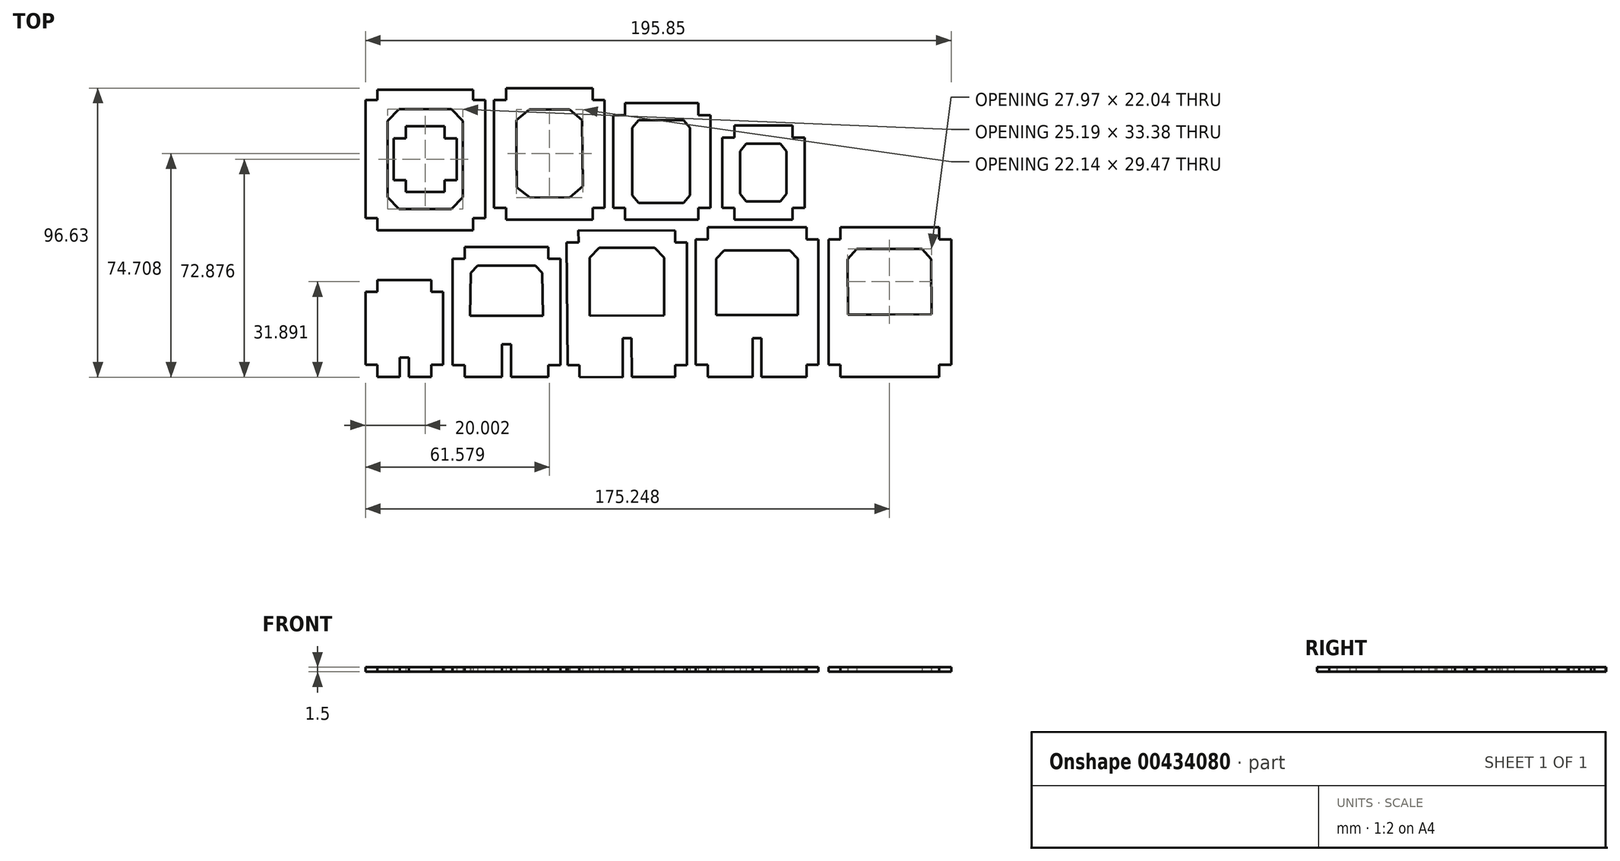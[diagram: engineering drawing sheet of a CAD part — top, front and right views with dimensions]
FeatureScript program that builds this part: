
annotation { "Feature Type Name" : "Feature", "Feature Type Description" : "" }
export const myFeature = defineFeature(function(context is Context, id is Id, definition is map)
    precondition{}
    {
        {
            var Q0;
            Q0=qCreatedBy(makeId("Top.planeOp"),FACE);
            var sketch = newSketch(context, id + "F0", { "sketchPlane" : qUnion([Q0])});
            skLineSegment(sketch, "E0", {"start": v(-112.3, 34.29) * mm, "end": v(-83.3, 34.29) * mm, "construction": true});
            skLineSegment(sketch, "E1", {"start": v(32.55, -18.26) * mm, "end": v(-0.45, -18.26) * mm, "construction": true});
            skLineSegment(sketch, "E2", {"start": v(-159.3, 74.29) * mm, "end": v(-159.3, 34.79) * mm, "construction": true});
            skLineSegment(sketch, "E3", {"start": v(-79.3, 38.29) * mm, "end": v(-79.3, 74.33) * mm, "construction": true});
            skLineSegment(sketch, "E4", {"start": v(-159.3, 74.29) * mm, "end": v(-155.3, 74.29) * mm, "construction": true});
            skLineSegment(sketch, "E5", {"start": v(-139.3, 78.29) * mm, "end": v(-139.3, 24.66) * mm, "construction": true});
            skPoint(sketch, "E5.endSnap0", {"position": v(-139.3, 74.29) * mm});
            skLineSegment(sketch, "E6", {"start": v(-155.3, 30.79) * mm, "end": v(-123.3, 30.79) * mm, "construction": true});
            skPoint(sketch, "E7.startSnap0", {"position": v(-118.3, 78.29) * mm});
            skLineSegment(sketch, "E8", {"start": v(-119.3, 74.29) * mm, "end": v(-119.3, 34.79) * mm, "construction": true});
            skPoint(sketch, "E9.0.start.orphan", {"position": v(-119.3, 78.29) * mm});
            skLineSegment(sketch, "E10.0", {"start": v(-155.3, 77.79) * mm, "end": v(-155.3, 74.29) * mm});
            skLineSegment(sketch, "E11", {"start": v(-155.3, 77.79) * mm, "end": v(-155.3, 74.29) * mm, "construction": true});
            skPoint(sketch, "E12.orphan", {"position": v(-155.3, -16.83) * mm});
            skLineSegment(sketch, "E13.trimOffspring", {"start": v(-155.3, 30.79) * mm, "end": v(-155.3, 30.48) * mm, "construction": true});
            skLineSegment(sketch, "E14.trimOffspring", {"start": v(-155.3, 30.79) * mm, "end": v(-155.3, 30.48) * mm});
            skLineSegment(sketch, "E15.MirrorCS", {"start": v(-123.3, 77.79) * mm, "end": v(-123.3, 74.29) * mm, "construction": true});
            skLineSegment(sketch, "E16.0", {"start": v(-159.3, 34.79) * mm, "end": v(-155.3, 34.79) * mm});
            skLineSegment(sketch, "E17", {"start": v(-155.3, 34.79) * mm, "end": v(-155.3, 30.48) * mm, "construction": true});
            skLineSegment(sketch, "E18", {"start": v(-123.3, 34.79) * mm, "end": v(-123.3, 30.79) * mm, "construction": true});
            skLineSegment(sketch, "E19.trimOffspring", {"start": v(-123.3, 34.79) * mm, "end": v(-119.3, 34.79) * mm});
            skLineSegment(sketch, "E20.trimOffspring", {"start": v(-123.3, 74.29) * mm, "end": v(-119.3, 74.29) * mm, "construction": true});
            skLineSegment(sketch, "E21", {"start": v(-139.3, 71.23) * mm, "end": v(-148.05, 71.23) * mm});
            skLineSegment(sketch, "E22", {"start": v(-148.05, 71.23) * mm, "end": v(-151.9, 67.31) * mm});
            skLineSegment(sketch, "E23", {"start": v(-151.9, 67.31) * mm, "end": v(-151.9, 54.54) * mm});
            skLineSegment(sketch, "E24", {"start": v(-119.3, 54.54) * mm, "end": v(-159.3, 54.54) * mm, "construction": true});
            skLineSegment(sketch, "E25.MirrorCS", {"start": v(-139.3, 71.23) * mm, "end": v(-130.55, 71.23) * mm});
            skLineSegment(sketch, "E26.MirrorCS", {"start": v(-130.55, 71.23) * mm, "end": v(-126.7, 67.31) * mm});
            skLineSegment(sketch, "E27.MirrorCS", {"start": v(-126.7, 67.31) * mm, "end": v(-126.7, 54.54) * mm});
            skLineSegment(sketch, "E28.MirrorCS", {"start": v(-139.3, 37.84) * mm, "end": v(-130.55, 37.84) * mm});
            skLineSegment(sketch, "E29.MirrorCS", {"start": v(-139.3, 37.84) * mm, "end": v(-148.05, 37.84) * mm});
            skLineSegment(sketch, "E30.MirrorCS", {"start": v(-148.05, 37.84) * mm, "end": v(-151.9, 41.76) * mm});
            skLineSegment(sketch, "E31.MirrorCS", {"start": v(-151.9, 41.76) * mm, "end": v(-151.9, 54.54) * mm});
            skLineSegment(sketch, "E32.MirrorCS", {"start": v(-126.7, 41.76) * mm, "end": v(-126.7, 54.54) * mm});
            skLineSegment(sketch, "E33.MirrorCS", {"start": v(-130.55, 37.84) * mm, "end": v(-126.7, 41.76) * mm});
            skLineSegment(sketch, "E34", {"start": v(-155.3, 77.79) * mm, "end": v(-123.3, 77.79) * mm});
            skLineSegment(sketch, "E35", {"start": v(-123.3, 74.29) * mm, "end": v(-119.3, 74.29) * mm});
            skLineSegment(sketch, "E36", {"start": v(-119.3, 34.79) * mm, "end": v(-123.3, 34.79) * mm});
            skLineSegment(sketch, "E37", {"start": v(-123.3, 30.79) * mm, "end": v(-155.3, 30.79) * mm});
            skLineSegment(sketch, "E38", {"start": v(-155.3, 34.79) * mm, "end": v(-159.3, 34.79) * mm});
            skLineSegment(sketch, "E39", {"start": v(-159.3, 74.29) * mm, "end": v(-159.3, 34.79) * mm});
            skLineSegment(sketch, "E40", {"start": v(-159.3, 74.29) * mm, "end": v(-155.3, 74.29) * mm});
            skLineSegment(sketch, "E41", {"start": v(-119.3, 74.29) * mm, "end": v(-119.3, 34.79) * mm});
            skLineSegment(sketch, "E42", {"start": v(-123.3, 74.29) * mm, "end": v(-123.3, 77.79) * mm});
            skLineSegment(sketch, "E43", {"start": v(-123.3, 34.79) * mm, "end": v(-123.3, 30.79) * mm});
            skLineSegment(sketch, "E44", {"start": v(-155.3, 34.79) * mm, "end": v(-155.3, 30.79) * mm});
            skLineSegment(sketch, "E45.0", {"start": v(-83.3, 34.29) * mm, "end": v(-83.3, 38.29) * mm});
            skLineSegment(sketch, "E46", {"start": v(-116.3, 74.29) * mm, "end": v(-112.3, 74.3) * mm, "construction": true});
            skLineSegment(sketch, "E47", {"start": v(-116.3, 74.29) * mm, "end": v(-116.3, 38.29) * mm, "construction": true});
            skLineSegment(sketch, "E48.0", {"start": v(-112.3, 78.29) * mm, "end": v(-112.3, 74.3) * mm});
            skLineSegment(sketch, "E49.0", {"start": v(-116.3, 38.29) * mm, "end": v(-112.3, 38.29) * mm});
            skPoint(sketch, "E50.orphan", {"position": v(-113.67, 34.29) * mm});
            skLineSegment(sketch, "E51.trimOffspring", {"start": v(-112.3, 38.29) * mm, "end": v(-112.3, 34.29) * mm});
            skLineSegment(sketch, "E52.trimOffspring", {"start": v(-83.3, 74.33) * mm, "end": v(-83.3, 78.29) * mm});
            skLineSegment(sketch, "E53.trimOffspring", {"start": v(-83.3, 38.29) * mm, "end": v(-79.3, 38.29) * mm});
            skLineSegment(sketch, "E54", {"start": v(-83.3, 34.29) * mm, "end": v(-112.3, 34.29) * mm});
            skLineSegment(sketch, "E55", {"start": v(-112.3, 38.29) * mm, "end": v(-116.3, 38.29) * mm});
            skLineSegment(sketch, "E56", {"start": v(-116.3, 38.29) * mm, "end": v(-116.3, 74.29) * mm});
            skLineSegment(sketch, "E57", {"start": v(-116.3, 74.29) * mm, "end": v(-112.3, 74.3) * mm});
            skLineSegment(sketch, "E58", {"start": v(-112.3, 78.29) * mm, "end": v(-83.3, 78.29) * mm});
            skLineSegment(sketch, "E59", {"start": v(-83.3, 74.33) * mm, "end": v(-79.3, 74.33) * mm});
            skLineSegment(sketch, "E60", {"start": v(-79.3, 74.33) * mm, "end": v(-79.3, 38.75) * mm});
            skLineSegment(sketch, "E61.trimOffspring", {"start": v(-83.3, 74.33) * mm, "end": v(-79.3, 74.33) * mm, "construction": true});
            skPoint(sketch, "E62.orphan", {"position": v(-77.3, 78.29) * mm});
            skLineSegment(sketch, "E63.trimOffspring", {"start": v(-112.3, 78.29) * mm, "end": v(-83.3, 78.29) * mm, "construction": true});
            skLineSegment(sketch, "E64", {"start": v(-97.8, 78.29) * mm, "end": v(-97.8, 34.29) * mm, "construction": true});
            skLineSegment(sketch, "E65", {"start": v(-97.8, 71.1) * mm, "end": v(-104.49, 71.1) * mm});
            skLineSegment(sketch, "E66", {"start": v(-104.49, 71.1) * mm, "end": v(-108.79, 67.53) * mm});
            skLineSegment(sketch, "E67", {"start": v(-108.79, 67.53) * mm, "end": v(-108.79, 56.34) * mm});
            skLineSegment(sketch, "E68.MirrorCS", {"start": v(-97.8, 71.1) * mm, "end": v(-91.1, 71.1) * mm});
            skLineSegment(sketch, "E69.MirrorCS", {"start": v(-91.1, 71.1) * mm, "end": v(-86.8, 67.53) * mm});
            skPoint(sketch, "E70.start.orphan", {"position": v(-79.3, 58.29) * mm});
            skLineSegment(sketch, "E71", {"start": v(-116.3, 56.29) * mm, "end": v(-79.3, 56.54) * mm, "construction": true});
            skPoint(sketch, "E72.MirrorCS.end.orphan", {"position": v(-86.8, 58.29) * mm});
            skPoint(sketch, "E72.MirrorCS.start.orphan", {"position": v(-86.8, 67.53) * mm});
            skLineSegment(sketch, "E73", {"start": v(-86.8, 67.53) * mm, "end": v(-86.73, 56.49) * mm});
            skPoint(sketch, "E74.orphan", {"position": v(-108.79, 58.29) * mm});
            skLineSegment(sketch, "E75.MirrorCS", {"start": v(-97.6, 41.72) * mm, "end": v(-90.9, 41.82) * mm});
            skLineSegment(sketch, "E76.MirrorCS", {"start": v(-90.9, 41.82) * mm, "end": v(-86.65, 45.45) * mm});
            skLineSegment(sketch, "E77.MirrorCS", {"start": v(-86.65, 45.45) * mm, "end": v(-86.73, 56.49) * mm});
            skLineSegment(sketch, "E78.MirrorCS", {"start": v(-97.6, 41.72) * mm, "end": v(-104.29, 41.63) * mm});
            skLineSegment(sketch, "E79.MirrorCS", {"start": v(-104.29, 41.63) * mm, "end": v(-108.64, 45.15) * mm});
            skLineSegment(sketch, "E80.MirrorCS", {"start": v(-108.64, 45.15) * mm, "end": v(-108.79, 56.34) * mm});
            skLineSegment(sketch, "E81", {"start": v(-76.47, 69.29) * mm, "end": v(-76.47, 38.29) * mm, "construction": true});
            skLineSegment(sketch, "E82", {"start": v(-43.97, 69.29) * mm, "end": v(-43.97, 38.29) * mm, "construction": true});
            skLineSegment(sketch, "E83", {"start": v(-72.47, 73.29) * mm, "end": v(-48.45, 73.29) * mm, "construction": true});
            skLineSegment(sketch, "E84.trimOffspring", {"start": v(-76.47, 38.29) * mm, "end": v(-72.47, 38.29) * mm});
            skLineSegment(sketch, "E85.0", {"start": v(-47.97, 69.29) * mm, "end": v(-43.97, 69.29) * mm});
            skLineSegment(sketch, "E86.0", {"start": v(-72.47, 73.29) * mm, "end": v(-72.47, 69.29) * mm});
            skLineSegment(sketch, "E87.0", {"start": v(-47.97, 73.29) * mm, "end": v(-47.97, 69.29) * mm});
            skLineSegment(sketch, "E88.trimOffspring", {"start": v(-72.47, 34.29) * mm, "end": v(-47.97, 34.29) * mm, "construction": true});
            skLineSegment(sketch, "E89.trimOffspring", {"start": v(-47.97, 38.29) * mm, "end": v(-43.97, 38.29) * mm});
            skLineSegment(sketch, "E90.trimOffspring", {"start": v(-72.47, 38.29) * mm, "end": v(-72.47, 34.29) * mm});
            skLineSegment(sketch, "E91.trimOffspring", {"start": v(-47.97, 38.29) * mm, "end": v(-47.97, 34.29) * mm});
            skLineSegment(sketch, "E92.trimOffspring", {"start": v(-76.47, 69.29) * mm, "end": v(-72.47, 69.29) * mm});
            skLineSegment(sketch, "E93", {"start": v(-72.47, 73.29) * mm, "end": v(-48.45, 73.29) * mm});
            skLineSegment(sketch, "E94", {"start": v(-43.97, 69.29) * mm, "end": v(-43.97, 38.29) * mm});
            skLineSegment(sketch, "E95", {"start": v(-76.47, 69.29) * mm, "end": v(-76.47, 38.29) * mm});
            skLineSegment(sketch, "E96", {"start": v(-72.47, 34.29) * mm, "end": v(-47.97, 34.29) * mm});
            skPoint(sketch, "E97.orphan", {"position": v(-76.47, 69.98) * mm});
            skPoint(sketch, "E98.endSnap0", {"position": v(-41.2, 34.29) * mm});
            skLineSegment(sketch, "E99", {"start": v(-39.98, 61.57) * mm, "end": v(-39.98, 38.29) * mm, "construction": true});
            skLineSegment(sketch, "E100.0", {"start": v(-35.98, 34.29) * mm, "end": v(-35.98, 38.29) * mm});
            skLineSegment(sketch, "E101.0", {"start": v(-16.48, 34.29) * mm, "end": v(-16.48, 38.29) * mm});
            skLineSegment(sketch, "E102.0", {"start": v(-39.98, 61.79) * mm, "end": v(-35.98, 61.79) * mm});
            skLineSegment(sketch, "E103.0", {"start": v(-39.98, 38.29) * mm, "end": v(-35.98, 38.29) * mm});
            skPoint(sketch, "E104.orphan", {"position": v(-9.95, 34.29) * mm});
            skLineSegment(sketch, "E105.trimOffspring", {"start": v(-12.48, 38.29) * mm, "end": v(-12.48, 61.79) * mm});
            skLineSegment(sketch, "E106.trimOffspring", {"start": v(-35.98, 65.79) * mm, "end": v(-16.48, 65.79) * mm});
            skLineSegment(sketch, "E107.trimOffspring", {"start": v(-35.98, 61.79) * mm, "end": v(-35.98, 65.79) * mm});
            skLineSegment(sketch, "E108.trimOffspring", {"start": v(-16.48, 61.79) * mm, "end": v(-12.48, 61.79) * mm});
            skLineSegment(sketch, "E109.trimOffspring", {"start": v(-16.48, 61.79) * mm, "end": v(-16.48, 65.79) * mm});
            skLineSegment(sketch, "E110.trimOffspring", {"start": v(-35.98, 34.29) * mm, "end": v(-16.48, 34.29) * mm, "construction": true});
            skLineSegment(sketch, "E111.trimOffspring", {"start": v(-39.98, 38.29) * mm, "end": v(-39.98, 61.79) * mm, "construction": true});
            skLineSegment(sketch, "E112.trimOffspring", {"start": v(-16.48, 38.29) * mm, "end": v(-12.48, 38.29) * mm});
            skLineSegment(sketch, "E113", {"start": v(-35.98, 34.29) * mm, "end": v(-16.48, 34.29) * mm});
            skPoint(sketch, "E114.orphan", {"position": v(-43.97, 34.29) * mm});
            skPoint(sketch, "E115.orphan", {"position": v(-43.97, 69.68) * mm});
            skLineSegment(sketch, "E116", {"start": v(-60.46, 73.29) * mm, "end": v(-60.46, 34.29) * mm, "construction": true});
            skLineSegment(sketch, "E117", {"start": v(-76.47, 53.79) * mm, "end": v(-43.97, 53.79) * mm, "construction": true});
            skLineSegment(sketch, "E118", {"start": v(-60.46, 67.64) * mm, "end": v(-67.94, 67.64) * mm});
            skLineSegment(sketch, "E119", {"start": v(-67.94, 67.64) * mm, "end": v(-70.13, 65.1) * mm});
            skLineSegment(sketch, "E120", {"start": v(-70.13, 65.1) * mm, "end": v(-70.13, 53.79) * mm});
            skLineSegment(sketch, "E121.MirrorCS", {"start": v(-60.46, 67.64) * mm, "end": v(-52.98, 67.64) * mm});
            skLineSegment(sketch, "E122.MirrorCS", {"start": v(-52.98, 67.64) * mm, "end": v(-50.79, 65.1) * mm});
            skLineSegment(sketch, "E123.MirrorCS", {"start": v(-50.79, 65.1) * mm, "end": v(-50.79, 53.79) * mm});
            skLineSegment(sketch, "E124.MirrorCS", {"start": v(-60.46, 39.94) * mm, "end": v(-67.94, 39.94) * mm});
            skLineSegment(sketch, "E125.MirrorCS", {"start": v(-67.94, 39.94) * mm, "end": v(-70.13, 42.47) * mm});
            skLineSegment(sketch, "E126.MirrorCS", {"start": v(-70.13, 42.47) * mm, "end": v(-70.13, 53.79) * mm});
            skLineSegment(sketch, "E127.MirrorCS", {"start": v(-60.46, 39.94) * mm, "end": v(-52.98, 39.94) * mm});
            skLineSegment(sketch, "E128.MirrorCS", {"start": v(-52.98, 39.94) * mm, "end": v(-50.79, 42.47) * mm});
            skLineSegment(sketch, "E129.MirrorCS", {"start": v(-50.79, 42.47) * mm, "end": v(-50.79, 53.79) * mm});
            skLineSegment(sketch, "E130", {"start": v(-26.23, 65.79) * mm, "end": v(-26.23, 34.29) * mm, "construction": true});
            skLineSegment(sketch, "E131", {"start": v(-39.98, 50.04) * mm, "end": v(-12.48, 50.04) * mm, "construction": true});
            skLineSegment(sketch, "E132", {"start": v(-26.23, 59.72) * mm, "end": v(-31.94, 59.72) * mm});
            skLineSegment(sketch, "E133", {"start": v(-31.94, 59.72) * mm, "end": v(-33.96, 57.19) * mm});
            skLineSegment(sketch, "E134", {"start": v(-33.96, 57.19) * mm, "end": v(-33.96, 50.04) * mm});
            skLineSegment(sketch, "E135.MirrorCS", {"start": v(-26.23, 59.72) * mm, "end": v(-20.52, 59.72) * mm});
            skLineSegment(sketch, "E136.MirrorCS", {"start": v(-20.52, 59.72) * mm, "end": v(-18.5, 57.19) * mm});
            skLineSegment(sketch, "E137.MirrorCS", {"start": v(-18.5, 57.19) * mm, "end": v(-18.5, 50.04) * mm});
            skLineSegment(sketch, "E138.MirrorCS", {"start": v(-20.52, 40.35) * mm, "end": v(-18.5, 42.89) * mm});
            skLineSegment(sketch, "E139.MirrorCS", {"start": v(-26.23, 40.35) * mm, "end": v(-20.52, 40.35) * mm});
            skLineSegment(sketch, "E140.MirrorCS", {"start": v(-26.23, 40.35) * mm, "end": v(-31.94, 40.35) * mm});
            skLineSegment(sketch, "E141.MirrorCS", {"start": v(-31.94, 40.35) * mm, "end": v(-33.96, 42.89) * mm});
            skLineSegment(sketch, "E142.MirrorCS", {"start": v(-33.96, 42.89) * mm, "end": v(-33.96, 50.04) * mm});
            skLineSegment(sketch, "E143.MirrorCS", {"start": v(-18.5, 42.89) * mm, "end": v(-18.5, 50.04) * mm});
            skPoint(sketch, "E144.orphan", {"position": v(-116.3, 34.29) * mm});
            skLineSegment(sketch, "E145", {"start": v(-146.08, 65.54) * mm, "end": v(-133.05, 65.54) * mm, "construction": true});
            skLineSegment(sketch, "E146", {"start": v(-149.8, 47.54) * mm, "end": v(-149.8, 61.54) * mm, "construction": true});
            skPoint(sketch, "E146.endSnap0", {"position": v(-151.9, 60.92) * mm});
            skLineSegment(sketch, "E147.MirrorCS", {"start": v(-128.8, 47.54) * mm, "end": v(-128.8, 61.54) * mm, "construction": true});
            skLineSegment(sketch, "E148.MirrorCS", {"start": v(-146.08, 43.54) * mm, "end": v(-133.05, 43.54) * mm, "construction": true});
            skLineSegment(sketch, "E149.0", {"start": v(-149.8, 61.54) * mm, "end": v(-145.8, 61.54) * mm});
            skLineSegment(sketch, "E150.0", {"start": v(-145.8, 43.54) * mm, "end": v(-145.8, 47.54) * mm});
            skPoint(sketch, "E151.orphan", {"position": v(-149.8, 60.92) * mm});
            skPoint(sketch, "E152.orphan", {"position": v(-128.8, 60.92) * mm});
            skLineSegment(sketch, "E153.MirrorCS", {"start": v(-149.8, 47.54) * mm, "end": v(-145.8, 47.54) * mm});
            skLineSegment(sketch, "E154.MirrorCS", {"start": v(-132.8, 43.54) * mm, "end": v(-132.8, 47.54) * mm});
            skLineSegment(sketch, "E155", {"start": v(-145.8, 65.54) * mm, "end": v(-133.05, 65.54) * mm});
            skLineSegment(sketch, "E156", {"start": v(-145.8, 43.54) * mm, "end": v(-132.8, 43.54) * mm});
            skLineSegment(sketch, "E157", {"start": v(-149.8, 61.54) * mm, "end": v(-149.8, 47.54) * mm});
            skLineSegment(sketch, "E158.trimOffspring", {"start": v(-132.8, 61.54) * mm, "end": v(-128.8, 61.54) * mm});
            skLineSegment(sketch, "E159.trimOffspring", {"start": v(-145.8, 61.54) * mm, "end": v(-145.8, 65.54) * mm});
            skLineSegment(sketch, "E160.trimOffspring", {"start": v(-132.8, 61.54) * mm, "end": v(-132.8, 65.54) * mm});
            skLineSegment(sketch, "E161.trimOffspring", {"start": v(-132.8, 47.54) * mm, "end": v(-128.8, 47.54) * mm});
            skPoint(sketch, "E162.orphan", {"position": v(-149.8, 46.48) * mm});
            skPoint(sketch, "E163.orphan", {"position": v(-128.8, 46.48) * mm});
            skLineSegment(sketch, "E164", {"start": v(-128.8, 61.54) * mm, "end": v(-128.8, 47.54) * mm});
            skPoint(sketch, "E165.orphan", {"position": v(-159.3, 30.79) * mm});
            skLineSegment(sketch, "E166.trimOffspring", {"start": v(-159.3, 10.17) * mm, "end": v(-159.3, -14.26) * mm, "construction": true});
            skPoint(sketch, "E167.orphan", {"position": v(-119.3, 30.79) * mm});
            skLineSegment(sketch, "E168", {"start": v(-133.3, 10.17) * mm, "end": v(-133.3, -14.26) * mm, "construction": true});
            skLineSegment(sketch, "E169", {"start": v(-130.14, -14.33) * mm, "end": v(-130.14, 21.17) * mm, "construction": true});
            skLineSegment(sketch, "E170.trimOffspring", {"start": v(-137.3, -18.26) * mm, "end": v(-144.8, -18.26) * mm, "construction": true});
            skLineSegment(sketch, "E171", {"start": v(-126.14, 25.17) * mm, "end": v(-98.14, 25.17) * mm, "construction": true});
            skLineSegment(sketch, "E172", {"start": v(-94.14, 21.17) * mm, "end": v(-94.14, -14.33) * mm, "construction": true});
            skLineSegment(sketch, "E173", {"start": v(-51.74, -14.33) * mm, "end": v(-51.74, 26.67) * mm, "construction": true});
            skPoint(sketch, "E174.orphan", {"position": v(-50.84, 30.67) * mm});
            skLineSegment(sketch, "E175", {"start": v(-44.85, 31.74) * mm, "end": v(-11.85, 31.74) * mm, "construction": true});
            skLineSegment(sketch, "E176", {"start": v(-7.85, 27.74) * mm, "end": v(-7.85, -14.26) * mm, "construction": true});
            skLineSegment(sketch, "E177", {"start": v(-48.85, 27.74) * mm, "end": v(-48.85, -14.26) * mm, "construction": true});
            skLineSegment(sketch, "E178", {"start": v(-4.45, 27.74) * mm, "end": v(-4.45, 25.1) * mm, "construction": true});
            skPoint(sketch, "E178.startSnap0", {"position": v(-4.45, 31.74) * mm});
            skLineSegment(sketch, "E179", {"start": v(36.55, 27.74) * mm, "end": v(36.55, -14.26) * mm, "construction": true});
            skPoint(sketch, "E180.orphan", {"position": v(-45.1, 31.74) * mm});
            skLineSegment(sketch, "E181", {"start": v(-4.45, 27.74) * mm, "end": v(-4.45, -14.26) * mm, "construction": true});
            skLineSegment(sketch, "E182.trimOffspring", {"start": v(-0.45, 31.74) * mm, "end": v(32.55, 31.74) * mm, "construction": true});
            skLineSegment(sketch, "E183.trimOffspring", {"start": v(-11.85, -18.26) * mm, "end": v(-26.85, -18.26) * mm, "construction": true});
            skLineSegment(sketch, "E184", {"start": v(-146.3, 14.17) * mm, "end": v(-146.3, -18.26) * mm, "construction": true});
            skLineSegment(sketch, "E185", {"start": v(-112.14, 25.17) * mm, "end": v(-112.14, -18.33) * mm, "construction": true});
            skLineSegment(sketch, "E186", {"start": v(-71.9, 30.67) * mm, "end": v(-71.74, -18.33) * mm, "construction": true});
            skLineSegment(sketch, "E187", {"start": v(-28.35, 31.74) * mm, "end": v(-28.35, -18.26) * mm, "construction": true});
            skLineSegment(sketch, "E188", {"start": v(15.88, 31.74) * mm, "end": v(16.05, -18.26) * mm, "construction": true});
            skLineSegment(sketch, "E189.0", {"start": v(-29.85, -5.26) * mm, "end": v(-29.85, -18.26) * mm, "construction": true});
            skLineSegment(sketch, "E190.0", {"start": v(-26.85, -5.26) * mm, "end": v(-26.85, -18.26) * mm});
            skLineSegment(sketch, "E191.0", {"start": v(-26.85, -5.26) * mm, "end": v(-29.85, -5.26) * mm, "construction": true});
            skLineSegment(sketch, "E192", {"start": v(-29.85, -18.26) * mm, "end": v(-29.85, -5.26) * mm});
            skLineSegment(sketch, "E193", {"start": v(-26.85, -5.26) * mm, "end": v(-29.85, -5.26) * mm});
            skLineSegment(sketch, "E194.trimOffspring", {"start": v(-29.85, -18.26) * mm, "end": v(-44.85, -18.26) * mm, "construction": true});
            skLineSegment(sketch, "E195.0", {"start": v(36.55, -14.26) * mm, "end": v(32.55, -14.26) * mm});
            skLineSegment(sketch, "E196.0", {"start": v(32.55, 31.74) * mm, "end": v(32.55, 27.74) * mm, "construction": true});
            skLineSegment(sketch, "E197.0", {"start": v(-4.45, 27.74) * mm, "end": v(-0.45, 27.74) * mm, "construction": true});
            skLineSegment(sketch, "E198.0", {"start": v(-0.45, 31.74) * mm, "end": v(-0.45, 27.74) * mm, "construction": true});
            skLineSegment(sketch, "E199.trimOffspring", {"start": v(32.55, 27.74) * mm, "end": v(36.55, 27.74) * mm, "construction": true});
            skLineSegment(sketch, "E200.trimOffspring", {"start": v(-0.45, -14.26) * mm, "end": v(-4.45, -14.26) * mm});
            skLineSegment(sketch, "E201.trimOffspring", {"start": v(-0.45, -14.26) * mm, "end": v(-0.45, -18.26) * mm, "construction": true});
            skLineSegment(sketch, "E202.trimOffspring", {"start": v(32.55, -14.26) * mm, "end": v(32.55, -18.26) * mm, "construction": true});
            skPoint(sketch, "E203.orphan", {"position": v(36.2, 31.74) * mm});
            skPoint(sketch, "E204.orphan", {"position": v(36.55, 31.74) * mm});
            skPoint(sketch, "E205.orphan", {"position": v(-4.45, -18.26) * mm});
            skPoint(sketch, "E206.orphan", {"position": v(36.55, -18.26) * mm});
            skLineSegment(sketch, "E207.0", {"start": v(-11.85, 31.74) * mm, "end": v(-11.85, 27.74) * mm});
            skLineSegment(sketch, "E208.0", {"start": v(-44.85, 31.74) * mm, "end": v(-44.85, 27.74) * mm});
            skLineSegment(sketch, "E209.0", {"start": v(-48.85, 27.74) * mm, "end": v(-44.85, 27.74) * mm, "construction": true});
            skLineSegment(sketch, "E210.0", {"start": v(-44.85, -14.26) * mm, "end": v(-48.85, -14.26) * mm, "construction": true});
            skLineSegment(sketch, "E211.0", {"start": v(-7.85, -14.26) * mm, "end": v(-11.85, -14.26) * mm, "construction": true});
            skLineSegment(sketch, "E212.trimOffspring", {"start": v(-11.85, 27.74) * mm, "end": v(-7.85, 27.74) * mm, "construction": true});
            skLineSegment(sketch, "E213.trimOffspring", {"start": v(-44.85, -14.26) * mm, "end": v(-44.85, -18.26) * mm});
            skPoint(sketch, "E214.orphan", {"position": v(-48.85, -18.26) * mm});
            skPoint(sketch, "E215.orphan", {"position": v(-48.85, 31.74) * mm});
            skPoint(sketch, "E216.orphan", {"position": v(-7.85, 31.74) * mm});
            skLineSegment(sketch, "E217", {"start": v(-44.85, -18.26) * mm, "end": v(-29.85, -18.26) * mm});
            skLineSegment(sketch, "E218", {"start": v(-48.85, 27.74) * mm, "end": v(-48.85, -14.26) * mm});
            skLineSegment(sketch, "E219", {"start": v(-48.85, -14.26) * mm, "end": v(-44.85, -14.26) * mm});
            skLineSegment(sketch, "E220", {"start": v(-11.85, -14.26) * mm, "end": v(-7.85, -14.26) * mm});
            skLineSegment(sketch, "E221", {"start": v(-7.85, -14.26) * mm, "end": v(-7.85, 27.74) * mm});
            skLineSegment(sketch, "E222", {"start": v(-7.85, 27.74) * mm, "end": v(-11.85, 27.74) * mm});
            skLineSegment(sketch, "E223", {"start": v(-44.85, 31.74) * mm, "end": v(-11.85, 31.74) * mm});
            skPoint(sketch, "E224.orphan", {"position": v(-7.85, -18.26) * mm});
            skLineSegment(sketch, "E225.trimOffspring", {"start": v(-11.85, -14.26) * mm, "end": v(-11.85, -18.26) * mm});
            skLineSegment(sketch, "E226.trimOffspring", {"start": v(-26.85, -18.26) * mm, "end": v(-11.85, -18.26) * mm});
            skLineSegment(sketch, "E227", {"start": v(-0.45, 31.74) * mm, "end": v(32.55, 31.74) * mm});
            skLineSegment(sketch, "E228", {"start": v(32.55, 27.74) * mm, "end": v(36.55, 27.74) * mm});
            skLineSegment(sketch, "E229", {"start": v(36.55, 27.74) * mm, "end": v(36.55, -14.26) * mm});
            skLineSegment(sketch, "E230", {"start": v(-0.45, -18.26) * mm, "end": v(32.55, -18.26) * mm});
            skLineSegment(sketch, "E231", {"start": v(32.55, -18.26) * mm, "end": v(32.55, -14.26) * mm});
            skLineSegment(sketch, "E232", {"start": v(-0.45, -18.26) * mm, "end": v(-0.45, -14.26) * mm});
            skLineSegment(sketch, "E233", {"start": v(-4.45, -14.26) * mm, "end": v(-4.45, 27.74) * mm});
            skLineSegment(sketch, "E234", {"start": v(-0.45, 27.74) * mm, "end": v(-0.45, 31.74) * mm});
            skLineSegment(sketch, "E235", {"start": v(-44.85, 27.74) * mm, "end": v(-48.85, 27.74) * mm});
            skLineSegment(sketch, "E236", {"start": v(-0.45, 27.74) * mm, "end": v(-4.45, 27.74) * mm});
            skLineSegment(sketch, "E237", {"start": v(32.55, 27.74) * mm, "end": v(32.55, 31.74) * mm});
            skLineSegment(sketch, "E238", {"start": v(-84.25, 2.24) * mm, "end": v(-59.37, 2.32) * mm, "construction": true});
            skLineSegment(sketch, "E239", {"start": v(2.03, 2.53) * mm, "end": v(1.96, 21.04) * mm});
            skLineSegment(sketch, "E240", {"start": v(1.96, 21.04) * mm, "end": v(4.95, 24.5) * mm});
            skLineSegment(sketch, "E241", {"start": v(4.95, 24.5) * mm, "end": v(15.9, 24.5) * mm});
            skLineSegment(sketch, "E242", {"start": v(2.03, 2.53) * mm, "end": v(15.98, 2.53) * mm});
            skLineSegment(sketch, "E243.trimOffspring", {"start": v(2.03, 2.53) * mm, "end": v(28.82, 2.62) * mm, "construction": true});
            skLineSegment(sketch, "E244.trimOffspring", {"start": v(-42.03, 2.38) * mm, "end": v(-28.35, 2.43) * mm, "construction": true});
            skLineSegment(sketch, "E245.MirrorCS", {"start": v(29.93, 2.63) * mm, "end": v(15.98, 2.53) * mm});
            skLineSegment(sketch, "E246.MirrorCS", {"start": v(29.93, 2.63) * mm, "end": v(29.86, 21.14) * mm});
            skLineSegment(sketch, "E247.MirrorCS", {"start": v(29.86, 21.14) * mm, "end": v(26.86, 24.57) * mm});
            skLineSegment(sketch, "E248", {"start": v(-28.35, 2.43) * mm, "end": v(-42.03, 2.38) * mm});
            skLineSegment(sketch, "E249", {"start": v(-42.03, 21.2) * mm, "end": v(-39.35, 24.04) * mm});
            skLineSegment(sketch, "E250", {"start": v(-39.35, 24.04) * mm, "end": v(-28.35, 24.04) * mm});
            skPoint(sketch, "E251.orphan", {"position": v(-48.85, 2.36) * mm});
            skPoint(sketch, "E252.orphan", {"position": v(-7.85, 2.5) * mm});
            skLineSegment(sketch, "E253.MirrorCS", {"start": v(-14.66, 2.38) * mm, "end": v(-28.35, 2.43) * mm, "construction": true});
            skLineSegment(sketch, "E254.MirrorCS", {"start": v(-14.66, 21.2) * mm, "end": v(-17.34, 24.04) * mm});
            skLineSegment(sketch, "E255.MirrorCS", {"start": v(-17.34, 24.04) * mm, "end": v(-28.35, 24.04) * mm});
            skLineSegment(sketch, "E256", {"start": v(-28.35, 2.43) * mm, "end": v(-14.66, 2.38) * mm});
            skLineSegment(sketch, "E257", {"start": v(-112.14, 2.16) * mm, "end": v(-99.98, 2.16) * mm});
            skLineSegment(sketch, "E258", {"start": v(-99.98, 2.16) * mm, "end": v(-100.17, 16.46) * mm});
            skLineSegment(sketch, "E259", {"start": v(-100.17, 16.46) * mm, "end": v(-102.54, 19) * mm});
            skLineSegment(sketch, "E260", {"start": v(-102.54, 19) * mm, "end": v(-112.14, 19) * mm});
            skLineSegment(sketch, "E261.MirrorCS", {"start": v(-121.75, 19) * mm, "end": v(-112.14, 19) * mm});
            skLineSegment(sketch, "E262", {"start": v(-124.3, 2.16) * mm, "end": v(-112.14, 2.16) * mm});
            skLineSegment(sketch, "E263.trimOffspring", {"start": v(-99.98, 2.16) * mm, "end": v(-124.3, 2.16) * mm, "construction": true});
            skLineSegment(sketch, "E264", {"start": v(-84.32, 21.56) * mm, "end": v(-81.19, 24.85) * mm});
            skLineSegment(sketch, "E265", {"start": v(-81.19, 24.85) * mm, "end": v(-71.89, 24.85) * mm});
            skLineSegment(sketch, "E266.MirrorCS", {"start": v(-62.58, 24.91) * mm, "end": v(-71.89, 24.85) * mm});
            skLineSegment(sketch, "E267.MirrorCS", {"start": v(-59.43, 21.65) * mm, "end": v(-62.58, 24.91) * mm});
            skLineSegment(sketch, "E268.MirrorCS", {"start": v(-59.37, 2.32) * mm, "end": v(-84.25, 2.24) * mm, "construction": true});
            skLineSegment(sketch, "E269", {"start": v(-84.25, 2.24) * mm, "end": v(-59.37, 2.32) * mm});
            skPoint(sketch, "E270.orphan", {"position": v(-91.88, 2.2) * mm});
            skPoint(sketch, "E271.orphan", {"position": v(-51.74, 2.35) * mm});
            skLineSegment(sketch, "E272.0", {"start": v(-51.74, -14.33) * mm, "end": v(-55.74, -14.33) * mm});
            skLineSegment(sketch, "E273.0", {"start": v(-87.74, -18.3) * mm, "end": v(-87.77, -14.33) * mm});
            skLineSegment(sketch, "E274.0", {"start": v(-55.74, -18.33) * mm, "end": v(-55.74, -14.33) * mm});
            skLineSegment(sketch, "E275.0", {"start": v(-92.07, 26.67) * mm, "end": v(-88.05, 26.67) * mm});
            skLineSegment(sketch, "E276", {"start": v(-51.74, 26.67) * mm, "end": v(-51.74, -14.33) * mm});
            skPoint(sketch, "E277.orphan", {"position": v(-92.07, 30.67) * mm});
            skPoint(sketch, "E278.orphan", {"position": v(-51.74, 30.67) * mm});
            skLineSegment(sketch, "E279.trimOffspring", {"start": v(-55.74, 26.67) * mm, "end": v(-51.74, 26.67) * mm});
            skLineSegment(sketch, "E280.trimOffspring", {"start": v(-55.74, 26.67) * mm, "end": v(-55.74, 30.67) * mm});
            skLineSegment(sketch, "E281.trimOffspring", {"start": v(-88.05, 26.67) * mm, "end": v(-88.07, 30.7) * mm});
            skLineSegment(sketch, "E282.trimOffspring", {"start": v(-87.77, -14.33) * mm, "end": v(-91.74, -14.33) * mm});
            skLineSegment(sketch, "E283.0", {"start": v(-70.4, 30.67) * mm, "end": v(-70.4, 30.67) * mm});
            skLineSegment(sketch, "E284.0", {"start": v(-130.14, 21.17) * mm, "end": v(-126.14, 21.17) * mm});
            skLineSegment(sketch, "E285.0", {"start": v(-94.14, -14.33) * mm, "end": v(-98.14, -14.33) * mm});
            skLineSegment(sketch, "E286.0", {"start": v(-98.14, 25.17) * mm, "end": v(-98.14, 21.17) * mm});
            skLineSegment(sketch, "E287.0", {"start": v(-126.14, -18.33) * mm, "end": v(-126.14, -14.33) * mm, "construction": true});
            skLineSegment(sketch, "E288", {"start": v(-126.14, 25.17) * mm, "end": v(-98.14, 25.17) * mm});
            skLineSegment(sketch, "E289", {"start": v(-94.14, 21.17) * mm, "end": v(-94.14, -14.33) * mm});
            skLineSegment(sketch, "E290", {"start": v(-130.14, 21.17) * mm, "end": v(-130.14, -14.33) * mm});
            skLineSegment(sketch, "E291.trimOffspring", {"start": v(-98.14, 21.17) * mm, "end": v(-94.14, 21.17) * mm});
            skLineSegment(sketch, "E292.trimOffspring", {"start": v(-98.14, -14.33) * mm, "end": v(-98.14, -18.33) * mm});
            skLineSegment(sketch, "E293.trimOffspring", {"start": v(-126.14, 21.17) * mm, "end": v(-126.14, 25.17) * mm, "construction": true});
            skLineSegment(sketch, "E294.trimOffspring", {"start": v(-73.24, -18.33) * mm, "end": v(-75.53, -18.33) * mm, "construction": true});
            skPoint(sketch, "E295.orphan", {"position": v(-51.74, -18.33) * mm});
            skLineSegment(sketch, "E296", {"start": v(-70.24, -18.33) * mm, "end": v(-55.74, -18.33) * mm});
            skLineSegment(sketch, "E297", {"start": v(-87.74, -18.3) * mm, "end": v(-73.24, -18.34) * mm});
            skLineSegment(sketch, "E298.0", {"start": v(-159.3, 10.17) * mm, "end": v(-155.3, 10.17) * mm});
            skLineSegment(sketch, "E299.0", {"start": v(-133.3, -14.26) * mm, "end": v(-137.3, -14.26) * mm});
            skLineSegment(sketch, "E300.trimOffspring", {"start": v(-137.3, 10.17) * mm, "end": v(-133.3, 10.17) * mm});
            skLineSegment(sketch, "E301.trimOffspring", {"start": v(-155.3, -14.26) * mm, "end": v(-155.3, -18.26) * mm});
            skLineSegment(sketch, "E302.trimOffspring", {"start": v(-155.3, -14.26) * mm, "end": v(-159.3, -14.26) * mm});
            skLineSegment(sketch, "E303", {"start": v(-133.3, 10.17) * mm, "end": v(-133.3, -14.26) * mm});
            skLineSegment(sketch, "E304", {"start": v(-159.3, 10.17) * mm, "end": v(-159.3, -14.26) * mm});
            skLineSegment(sketch, "E305", {"start": v(-155.3, -18.26) * mm, "end": v(-147.8, -18.26) * mm});
            skLineSegment(sketch, "E306.trimOffspring", {"start": v(-137.3, -14.26) * mm, "end": v(-137.3, -18.26) * mm});
            skPoint(sketch, "E307.orphan", {"position": v(-159.3, 14.17) * mm});
            skPoint(sketch, "E308.orphan", {"position": v(-133.3, 14.17) * mm});
            skPoint(sketch, "E309.orphan", {"position": v(-159.3, -18.26) * mm});
            skPoint(sketch, "E310.orphan", {"position": v(-133.3, -18.26) * mm});
            skLineSegment(sketch, "E311.0", {"start": v(-147.8, -11.76) * mm, "end": v(-147.8, -18.26) * mm});
            skLineSegment(sketch, "E312.0", {"start": v(-144.8, -11.76) * mm, "end": v(-144.8, -18.26) * mm});
            skLineSegment(sketch, "E313", {"start": v(-73.28, -5.33) * mm, "end": v(-70.28, -5.33) * mm, "construction": true});
            skLineSegment(sketch, "E314", {"start": v(-113.64, -7.33) * mm, "end": v(-110.64, -7.33) * mm, "construction": true});
            skLineSegment(sketch, "E315", {"start": v(-147.8, -11.76) * mm, "end": v(-144.8, -11.76) * mm, "construction": true});
            skLineSegment(sketch, "E316.trimOffspring", {"start": v(-110.64, -7.33) * mm, "end": v(-110.64, -18.33) * mm});
            skLineSegment(sketch, "E317.trimOffspring", {"start": v(-113.64, -7.33) * mm, "end": v(-113.64, -18.33) * mm});
            skPoint(sketch, "E318.orphan", {"position": v(-117.19, -7.33) * mm});
            skPoint(sketch, "E319.orphan", {"position": v(-79.13, -5.33) * mm});
            skLineSegment(sketch, "E320.trimOffspring", {"start": v(-73.28, -5.33) * mm, "end": v(-73.24, -18.34) * mm});
            skLineSegment(sketch, "E321.trimOffspring", {"start": v(-70.28, -5.33) * mm, "end": v(-70.24, -18.33) * mm});
            skPoint(sketch, "E322.orphan", {"position": v(-151.39, -11.76) * mm});
            skLineSegment(sketch, "E323.trimOffspring", {"start": v(-147.8, -18.26) * mm, "end": v(-155.3, -18.26) * mm, "construction": true});
            skLineSegment(sketch, "E324.trimOffspring", {"start": v(-144.8, -18.26) * mm, "end": v(-137.3, -18.26) * mm});
            skPoint(sketch, "E325.orphan", {"position": v(-94.14, -18.33) * mm});
            skPoint(sketch, "E326.orphan", {"position": v(-130.14, -18.33) * mm});
            skLineSegment(sketch, "E327", {"start": v(-126.14, -18.33) * mm, "end": v(-113.64, -18.33) * mm});
            skLineSegment(sketch, "E328.trimOffspring", {"start": v(-126.14, -14.33) * mm, "end": v(-130.14, -14.33) * mm});
            skLineSegment(sketch, "E329", {"start": v(-110.64, -18.33) * mm, "end": v(-98.14, -18.33) * mm});
            skLineSegment(sketch, "E330", {"start": v(-113.64, -7.33) * mm, "end": v(-110.64, -7.33) * mm});
            skLineSegment(sketch, "E331", {"start": v(-144.8, -11.76) * mm, "end": v(-147.8, -11.76) * mm});
            skPoint(sketch, "E332.MirrorCS.end.orphan", {"position": v(-59.43, 21.65) * mm});
            skPoint(sketch, "E333.MirrorCS.end.orphan", {"position": v(-14.66, 21.2) * mm});
            skPoint(sketch, "E333.MirrorCS.start.orphan", {"position": v(-14.66, 2.38) * mm});
            skPoint(sketch, "E334.orphan", {"position": v(-94.14, 25.17) * mm});
            skPoint(sketch, "E335.orphan", {"position": v(-130.14, 25.17) * mm});
            skLineSegment(sketch, "E336", {"start": v(-88.07, 30.7) * mm, "end": v(-55.74, 30.67) * mm});
            skPoint(sketch, "E337.MirrorCS.end.orphan", {"position": v(-124.12, 16.46) * mm});
            skPoint(sketch, "E338.MirrorCS.end.orphan", {"position": v(-121.75, 19) * mm});
            skLineSegment(sketch, "E339.MirrorCS", {"start": v(-124.12, 16.46) * mm, "end": v(-121.75, 19) * mm});
            skLineSegment(sketch, "E340.MirrorCS", {"start": v(-124.3, 2.16) * mm, "end": v(-124.12, 16.46) * mm});
            skLineSegment(sketch, "E341", {"start": v(-84.32, 21.56) * mm, "end": v(-84.25, 2.24) * mm});
            skLineSegment(sketch, "E342.MirrorCS", {"start": v(-59.43, 21.65) * mm, "end": v(-59.37, 2.32) * mm});
            skPoint(sketch, "E343.orphan", {"position": v(-116.3, 78.29) * mm});
            skPoint(sketch, "E344.orphan", {"position": v(-79.3, 78.29) * mm});
            skPoint(sketch, "E345.start.orphan", {"position": v(-159.3, 78.29) * mm});
            skLineSegment(sketch, "E346", {"start": v(-42.03, 2.38) * mm, "end": v(-42.03, 21.2) * mm});
            skLineSegment(sketch, "E347.MirrorCS", {"start": v(-14.66, 2.38) * mm, "end": v(-14.66, 21.2) * mm});
            skPoint(sketch, "E348.start.orphan", {"position": v(-91.74, -18.33) * mm});
            skLineSegment(sketch, "E349", {"start": v(-92.07, 26.67) * mm, "end": v(-91.74, -14.33) * mm});
            skLineSegment(sketch, "E350", {"start": v(15.9, 24.5) * mm, "end": v(26.86, 24.57) * mm});
            skPoint(sketch, "E351.MirrorCS.end.orphan", {"position": v(-79.3, 85.67) * mm});
            skPoint(sketch, "E351.MirrorCS.start.orphan", {"position": v(-116.3, 85.92) * mm});
            skLineSegment(sketch, "E352", {"start": v(-159.3, 0.74) * mm, "end": v(-136.84, 0.74) * mm, "construction": true});
            skCircle(sketch, "E353", {"center": v(-146.3, 0.74) * mm, "radius": 6.5 * mm});
            skCircle(sketch, "E354", {"center": v(-146.3, 0.74) * mm, "radius": 3.5 * mm});
            skLineSegment(sketch, "E355", {"start": v(-146.3, 0.74) * mm, "end": v(-140.6, 6.43) * mm, "construction": true});
            skLineSegment(sketch, "E356", {"start": v(-146.3, 0.74) * mm, "end": v(-154.57, -7.53) * mm, "construction": true});
            skLineSegment(sketch, "E357", {"start": v(-146.3, 0.74) * mm, "end": v(-150.3, 4.75) * mm, "construction": true});
            skLineSegment(sketch, "E358", {"start": v(-146.3, 0.74) * mm, "end": v(-138.2, -7.36) * mm, "construction": true});
            skCircle(sketch, "E359", {"center": v(-150.9, 5.34) * mm, "radius": 1 * mm});
            skCircle(sketch, "E360", {"center": v(-150.9, -3.86) * mm, "radius": 1 * mm});
            skCircle(sketch, "E361", {"center": v(-141.7, -3.86) * mm, "radius": 1 * mm});
            skCircle(sketch, "E362", {"center": v(-141.7, 5.34) * mm, "radius": 1 * mm});
            skPoint(sketch, "E363.0.start.orphan", {"position": v(-155.3, 14.17) * mm});
            skPoint(sketch, "E364.orphan", {"position": v(-164.38, 0.74) * mm});
            skLineSegment(sketch, "E365", {"start": v(-155.3, 10.17) * mm, "end": v(-155.3, 14.17) * mm});
            skLineSegment(sketch, "E366", {"start": v(-155.3, 14.17) * mm, "end": v(-137.3, 14.17) * mm});
            skLineSegment(sketch, "E367", {"start": v(-137.3, 14.17) * mm, "end": v(-137.3, 10.17) * mm});
            skPoint(sketch, "E368.orphan", {"position": v(-83.3, 80.82) * mm});
            skLineSegment(sketch, "E369", {"start": v(-112.3, 74.3) * mm, "end": v(-112.3, 78.29) * mm});
            skLineSegment(sketch, "E370", {"start": v(-83.3, 78.29) * mm, "end": v(-83.3, 74.33) * mm});
            skLineSegment(sketch, "E371", {"start": v(-79.3, 74.33) * mm, "end": v(-79.3, 38.29) * mm});
            skLineSegment(sketch, "E372", {"start": v(-47.97, 73.29) * mm, "end": v(-48.45, 73.29) * mm});
            skLineSegment(sketch, "E373", {"start": v(-39.98, 61.79) * mm, "end": v(-39.98, 61.57) * mm});
            skLineSegment(sketch, "E374", {"start": v(-39.98, 38.29) * mm, "end": v(-39.98, 61.79) * mm});
            skLineSegment(sketch, "E375", {"start": v(-73.28, -5.33) * mm, "end": v(-70.28, -5.33) * mm});
            skLineSegment(sketch, "E376", {"start": v(-126.14, 21.17) * mm, "end": v(-126.14, 25.17) * mm});
            skLineSegment(sketch, "E377", {"start": v(-126.14, -14.33) * mm, "end": v(-126.14, -18.33) * mm});
            skLineSegment(sketch, "E378", {"start": v(-124.12, 16.46) * mm, "end": v(-124.3, 2.16) * mm});
            skLineSegment(sketch, "E379", {"start": v(-121.75, 19) * mm, "end": v(-124.12, 16.46) * mm});
            skLineSegment(sketch, "E380", {"start": v(-121.75, 19) * mm, "end": v(-102.54, 19) * mm});
            skLineSegment(sketch, "E381", {"start": v(-126.14, 25.17) * mm, "end": v(-126.14, 21.17) * mm});
            skLineSegment(sketch, "E382", {"start": v(-126.14, 21.17) * mm, "end": v(-130.14, 21.17) * mm});
            skLineSegment(sketch, "E383", {"start": v(-130.14, -14.33) * mm, "end": v(-126.14, -14.33) * mm});
            skLineSegment(sketch, "E384", {"start": v(-113.64, -18.33) * mm, "end": v(-113.64, -7.33) * mm});
            skLineSegment(sketch, "E385", {"start": v(-98.14, -18.33) * mm, "end": v(-98.14, -14.33) * mm});
            skLineSegment(sketch, "E386", {"start": v(-98.14, -14.33) * mm, "end": v(-94.14, -14.33) * mm});
            skLineSegment(sketch, "E387", {"start": v(-99.98, 2.16) * mm, "end": v(-124.3, 2.16) * mm});
            skLineSegment(sketch, "E388", {"start": v(-145.8, 65.54) * mm, "end": v(-145.8, 61.54) * mm});
            skLineSegment(sketch, "E389", {"start": v(-132.8, 43.54) * mm, "end": v(-145.8, 43.54) * mm});
            skLineSegment(sketch, "E390", {"start": v(-145.8, 47.54) * mm, "end": v(-145.8, 43.54) * mm});
            skLineSegment(sketch, "E391", {"start": v(-145.8, 47.54) * mm, "end": v(-149.8, 47.54) * mm});
            skLineSegment(sketch, "E392", {"start": v(-132.8, 65.54) * mm, "end": v(-133.05, 65.54) * mm});
            skPoint(sketch, "E393.startDerivative.orphan", {"position": v(-175.35, 69.38) * mm});
            skSolve(sketch);
        }
        {
            var Q0;
            Q0=makeQuery(id+"F0.imprint","IMPRINT",FACE,{"disambiguationData":[TD([[makeQuery(id+"F0.imprint","IMPRINT",EDGE,{"derivedFrom":sQuery(id+"F0.wireOp",EDGE,"E10.0")}),1.0]])]});
            var Q1;
            Q1=makeQuery(id+"F0.imprint","IMPRINT",FACE,{"disambiguationData":[TD([[makeQuery(id+"F0.imprint","IMPRINT",EDGE,{"derivedFrom":sQuery(id+"F0.wireOp",EDGE,"E149.0")}),-1.0]])]});
            var Q2;
            Q2=makeQuery(id+"F0.imprint","IMPRINT",FACE,{"disambiguationData":[TD([[makeQuery(id+"F0.imprint","IMPRINT",EDGE,{"derivedFrom":sQuery(id+"F0.wireOp",EDGE,"E45.0")}),1.0]])]});
            var Q3;
            Q3=makeQuery(id+"F0.imprint","IMPRINT",FACE,{"disambiguationData":[TD([[makeQuery(id+"F0.imprint","IMPRINT",EDGE,{"derivedFrom":sQuery(id+"F0.wireOp",EDGE,"E84.trimOffspring")}),1.0]])]});
            var Q4;
            Q4=makeQuery(id+"F0.imprint","IMPRINT",FACE,{"disambiguationData":[TD([[makeQuery(id+"F0.imprint","IMPRINT",EDGE,{"derivedFrom":sQuery(id+"F0.wireOp",EDGE,"E100.0")}),-1.0]])]});
            var Q5;
            Q5=makeQuery(id+"F0.imprint","IMPRINT",FACE,{"disambiguationData":[TD([[makeQuery(id+"F0.imprint","IMPRINT",EDGE,{"derivedFrom":sQuery(id+"F0.wireOp",EDGE,"E259")}),-1.0]])]});
            var Q6;
            Q6=makeQuery(id+"F0.imprint","IMPRINT",FACE,{"disambiguationData":[TD([[makeQuery(id+"F0.imprint","IMPRINT",EDGE,{"derivedFrom":sQuery(id+"F0.wireOp",EDGE,"E264")}),1.0]])]});
            var Q7;
            Q7=makeQuery(id+"F0.imprint","IMPRINT",FACE,{"disambiguationData":[TD([[makeQuery(id+"F0.imprint","IMPRINT",EDGE,{"derivedFrom":sQuery(id+"F0.wireOp",EDGE,"E190.0")}),1.0]])]});
            var Q8;
            Q8=makeQuery(id+"F0.imprint","IMPRINT",FACE,{"disambiguationData":[TD([[makeQuery(id+"F0.imprint","IMPRINT",EDGE,{"derivedFrom":sQuery(id+"F0.wireOp",EDGE,"E195.0")}),-1.0]])]});
            var Q9;
            Q9=makeQuery(id+"F0.imprint","IMPRINT",FACE,{"disambiguationData":[TD([[makeQuery(id+"F0.imprint","IMPRINT",EDGE,{"derivedFrom":sQuery(id+"F0.wireOp",EDGE,"E298.0")}),-1.0]])]});
            var Q10;
            Q10=makeQuery(id+"F0.imprint","IMPRINT",FACE,{"disambiguationData":[TD([[makeQuery(id+"F0.imprint","IMPRINT",EDGE,{"derivedFrom":sQuery(id+"F0.wireOp",EDGE,"E354")}),-1.0]])]});
            var Q11;
            Q11=makeQuery(id+"F0.imprint","IMPRINT",FACE,{"disambiguationData":[TD([[makeQuery(id+"F0.imprint","IMPRINT",EDGE,{"derivedFrom":sQuery(id+"F0.wireOp",EDGE,"E354")}),1.0]])]});
            var Q12;
            {var subQ0=sQuery(id+"F0.wireOp",EDGE,"E362");var subQ1=sQuery(id+"F0.wireOp",EDGE,"E353");var subQ2=makeQuery(id+"F0.imprint","INTERSECT",VERTEX,{"disambiguationData":[OD(0.0)],"derivedFrom":[subQ1,subQ0]});Q12=makeQuery(id+"F0.imprint","IMPRINT",FACE,{"disambiguationData":[TD([[makeQuery(id+"F0.imprint","IMPRINT",EDGE,{"disambiguationData":[TD([[subQ2,1.0]])],"derivedFrom":subQ1}),1.0]])]});}
            var Q13;
            {var subQ0=sQuery(id+"F0.wireOp",EDGE,"E362");var subQ1=sQuery(id+"F0.wireOp",EDGE,"E353");var subQ2=makeQuery(id+"F0.imprint","INTERSECT",VERTEX,{"disambiguationData":[OD(0.0)],"derivedFrom":[subQ1,subQ0]});Q13=makeQuery(id+"F0.imprint","IMPRINT",FACE,{"disambiguationData":[TD([[makeQuery(id+"F0.imprint","IMPRINT",EDGE,{"disambiguationData":[TD([[subQ2,1.0]])],"derivedFrom":subQ1}),-1.0]])]});}
            var Q14;
            {var subQ0=sQuery(id+"F0.wireOp",EDGE,"E360");var subQ1=sQuery(id+"F0.wireOp",EDGE,"E353");var subQ2=makeQuery(id+"F0.imprint","INTERSECT",VERTEX,{"disambiguationData":[OD(0.0)],"derivedFrom":[subQ1,subQ0]});Q14=makeQuery(id+"F0.imprint","IMPRINT",FACE,{"disambiguationData":[TD([[makeQuery(id+"F0.imprint","IMPRINT",EDGE,{"disambiguationData":[TD([[subQ2,-1.0]])],"derivedFrom":subQ1}),-1.0]])]});}
            var Q15;
            {var subQ0=sQuery(id+"F0.wireOp",EDGE,"E360");var subQ1=sQuery(id+"F0.wireOp",EDGE,"E353");var subQ2=makeQuery(id+"F0.imprint","INTERSECT",VERTEX,{"disambiguationData":[OD(0.0)],"derivedFrom":[subQ1,subQ0]});Q15=makeQuery(id+"F0.imprint","IMPRINT",FACE,{"disambiguationData":[TD([[makeQuery(id+"F0.imprint","IMPRINT",EDGE,{"disambiguationData":[TD([[subQ2,-1.0]])],"derivedFrom":subQ1}),1.0]])]});}
            var Q16;
            {var subQ0=sQuery(id+"F0.wireOp",EDGE,"E361");var subQ1=sQuery(id+"F0.wireOp",EDGE,"E353");var subQ2=makeQuery(id+"F0.imprint","INTERSECT",VERTEX,{"disambiguationData":[OD(0.0)],"derivedFrom":[subQ1,subQ0]});Q16=makeQuery(id+"F0.imprint","IMPRINT",FACE,{"disambiguationData":[TD([[makeQuery(id+"F0.imprint","IMPRINT",EDGE,{"disambiguationData":[TD([[subQ2,-1.0]])],"derivedFrom":subQ1}),1.0]])]});}
            var Q17;
            {var subQ0=sQuery(id+"F0.wireOp",EDGE,"E361");var subQ1=sQuery(id+"F0.wireOp",EDGE,"E353");var subQ2=makeQuery(id+"F0.imprint","INTERSECT",VERTEX,{"disambiguationData":[OD(0.0)],"derivedFrom":[subQ1,subQ0]});Q17=makeQuery(id+"F0.imprint","IMPRINT",FACE,{"disambiguationData":[TD([[makeQuery(id+"F0.imprint","IMPRINT",EDGE,{"disambiguationData":[TD([[subQ2,-1.0]])],"derivedFrom":subQ1}),-1.0]])]});}
            var Q18;
            {var subQ0=sQuery(id+"F0.wireOp",EDGE,"E359");var subQ1=sQuery(id+"F0.wireOp",EDGE,"E353");var subQ2=makeQuery(id+"F0.imprint","INTERSECT",VERTEX,{"disambiguationData":[OD(0.0)],"derivedFrom":[subQ1,subQ0]});Q18=makeQuery(id+"F0.imprint","IMPRINT",FACE,{"disambiguationData":[TD([[makeQuery(id+"F0.imprint","IMPRINT",EDGE,{"disambiguationData":[TD([[subQ2,-1.0]])],"derivedFrom":subQ1}),-1.0]])]});}
            var Q19;
            {var subQ0=sQuery(id+"F0.wireOp",EDGE,"E359");var subQ1=sQuery(id+"F0.wireOp",EDGE,"E353");var subQ2=makeQuery(id+"F0.imprint","INTERSECT",VERTEX,{"disambiguationData":[OD(0.0)],"derivedFrom":[subQ1,subQ0]});Q19=makeQuery(id+"F0.imprint","IMPRINT",FACE,{"disambiguationData":[TD([[makeQuery(id+"F0.imprint","IMPRINT",EDGE,{"disambiguationData":[TD([[subQ2,-1.0]])],"derivedFrom":subQ1}),1.0]])]});}
            extrude(context, id + "F1", {"entities" : qUnion([Q0, Q1, Q2, Q3, Q4, Q5, Q6, Q7, Q8, Q9, Q10, Q11, Q12, Q13, Q14, Q15, Q16, Q17, Q18, Q19]), "depth" : 1.5 * mm, "offsetDistance" : 25 * mm});
        }
    });
